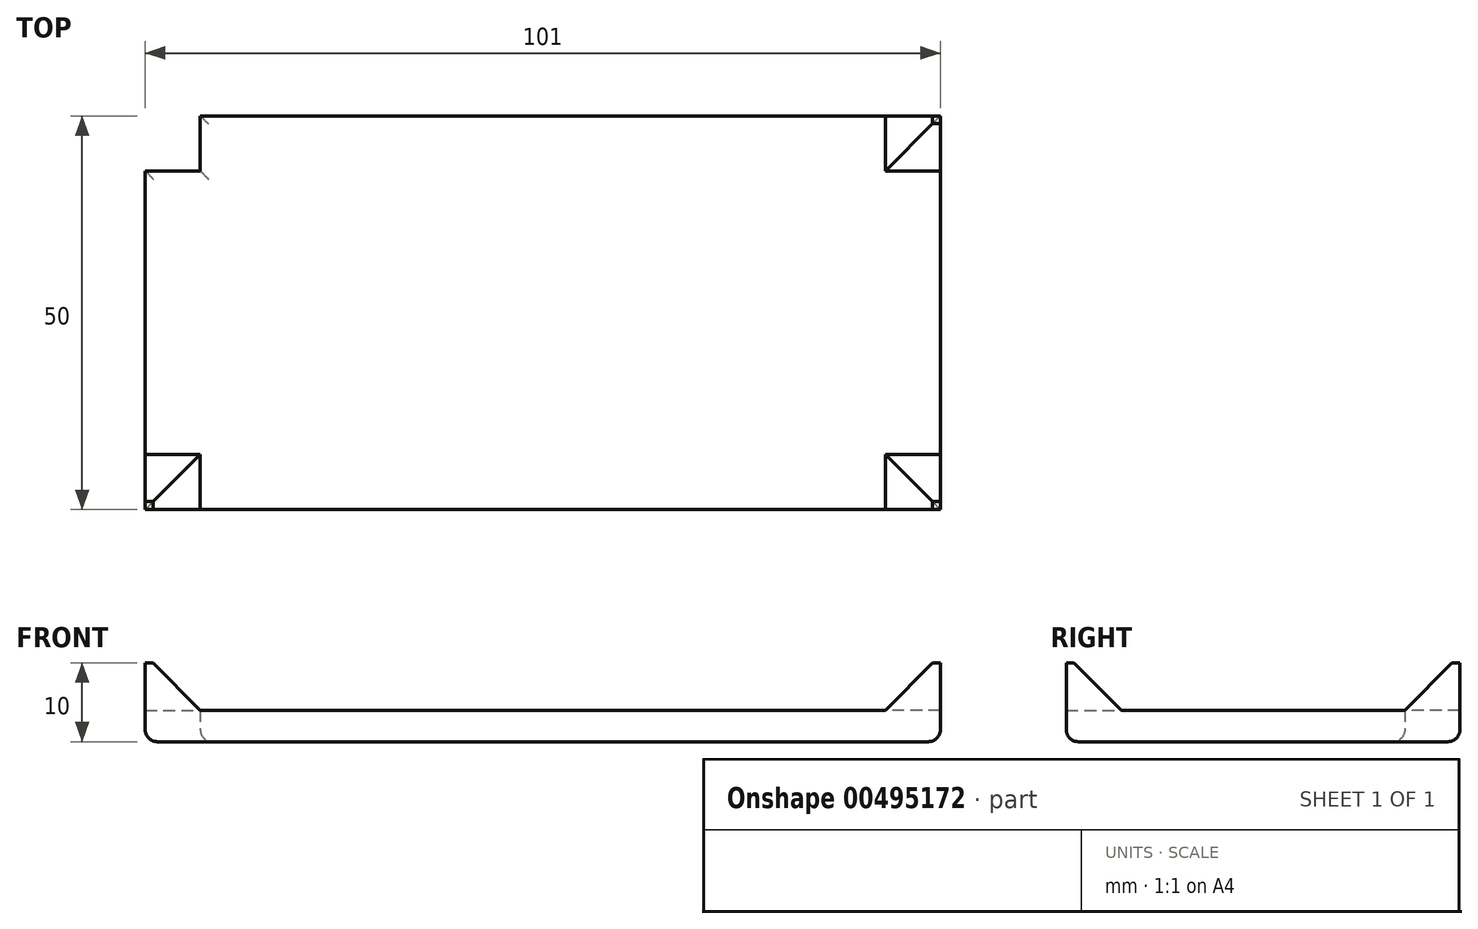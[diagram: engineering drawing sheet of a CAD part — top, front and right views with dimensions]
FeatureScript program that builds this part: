
annotation { "Feature Type Name" : "Feature", "Feature Type Description" : "" }
export const myFeature = defineFeature(function(context is Context, id is Id, definition is map)
    precondition{}
    {
        {
            var Q0;
            Q0=qCreatedBy(makeId("Top.planeOp"),FACE);
            var sketch = newSketch(context, id + "F0", { "sketchPlane" : qUnion([Q0])});
            skLineSegment(sketch, "E0.bottom", {"start": v(-50.5, 25) * mm, "end": v(50.5, 25) * mm});
            skLineSegment(sketch, "E0.top", {"start": v(-50.5, -25) * mm, "end": v(50.5, -25) * mm});
            skLineSegment(sketch, "E0.left", {"start": v(-50.5, 25) * mm, "end": v(-50.5, -25) * mm});
            skLineSegment(sketch, "E0.right", {"start": v(50.5, 25) * mm, "end": v(50.5, -25) * mm});
            skPoint(sketch, "E0.middle", {"position": v(0, 0) * mm});
            skLineSegment(sketch, "E1.bottom", {"start": v(-50.5, 25) * mm, "end": v(-43.5, 25) * mm});
            skLineSegment(sketch, "E1.top", {"start": v(-50.5, 18) * mm, "end": v(-43.5, 18) * mm});
            skLineSegment(sketch, "E1.left", {"start": v(-50.5, 25) * mm, "end": v(-50.5, 18) * mm});
            skLineSegment(sketch, "E1.right", {"start": v(-43.5, 25) * mm, "end": v(-43.5, 18) * mm});
            skLineSegment(sketch, "E2", {"start": v(-50.5, 18) * mm, "end": v(-50.5, 25) * mm, "construction": true});
            skLineSegment(sketch, "E3", {"start": v(-43.5, 25) * mm, "end": v(-50.5, 25) * mm, "construction": true});
            skLineSegment(sketch, "E4.MirrorCS", {"start": v(-50.5, -18) * mm, "end": v(-43.5, -18) * mm});
            skLineSegment(sketch, "E5.MirrorCS", {"start": v(-43.5, -25) * mm, "end": v(-43.5, -18) * mm});
            skLineSegment(sketch, "E6.MirrorCS", {"start": v(50.5, 18) * mm, "end": v(43.5, 18) * mm});
            skLineSegment(sketch, "E7.MirrorCS", {"start": v(43.5, 25) * mm, "end": v(43.5, 18) * mm});
            skLineSegment(sketch, "E8.MirrorCS", {"start": v(50.5, -18) * mm, "end": v(43.5, -18) * mm});
            skLineSegment(sketch, "E9.MirrorCS", {"start": v(43.5, -25) * mm, "end": v(43.5, -18) * mm});
            skSolve(sketch);
        }
        {
            var Q0;
            {var subQ3=sQuery(id+"F0.wireOp",EDGE,"E1.top");Q0=makeQuery(id+"F0.imprint","IMPRINT",FACE,{"disambiguationData":[TD([[makeQuery(id+"F0.imprint","IMPRINT",EDGE,{"derivedFrom":subQ3}),-1.0]])]});}
            extrude(context, id + "F1", {"entities" : qUnion([Q0]), "depth" : 4 * mm});
        }
        {
            var Q0;
            Q0=makeQuery(id+"F0.imprint","IMPRINT",FACE,{"disambiguationData":[TD([[makeQuery(id+"F0.imprint","IMPRINT",EDGE,{"derivedFrom":sQuery(id+"F0.wireOp",EDGE,"E1.bottom")}),-1.0]])]});
            var Q1;
            {var subQ4=sQuery(id+"F0.wireOp",EDGE,"E4.MirrorCS");Q1=makeQuery(id+"F0.imprint","IMPRINT",FACE,{"disambiguationData":[TD([[makeQuery(id+"F0.imprint","IMPRINT",EDGE,{"derivedFrom":subQ4}),-1.0]])]});}
            var Q2;
            {var subQ4=sQuery(id+"F0.wireOp",EDGE,"E6.MirrorCS");Q2=makeQuery(id+"F0.imprint","IMPRINT",FACE,{"disambiguationData":[TD([[makeQuery(id+"F0.imprint","IMPRINT",EDGE,{"derivedFrom":subQ4}),-1.0]])]});}
            var Q3;
            {var subQ4=sQuery(id+"F0.wireOp",EDGE,"E8.MirrorCS");Q3=makeQuery(id+"F0.imprint","IMPRINT",FACE,{"disambiguationData":[TD([[makeQuery(id+"F0.imprint","IMPRINT",EDGE,{"derivedFrom":subQ4}),1.0]])]});}
            extrude(context, id + "F2", {"entities" : qUnion([Q0, Q1, Q2, Q3]), "operationType" : NewBodyOperationType.ADD, "depth" : 10 * mm});
        }
        {
            var Q0;
            Q0=makeQuery(id+"F2.opExtrude","SWEPT_EDGE",EDGE,{"disambiguationData":[OSD([sQuery(id+"F0.wireOp",EDGE,"E1.top"),sQuery(id+"F0.wireOp",EDGE,"E1.right")])]});
            var Q1;
            Q1=makeQuery(id+"F2.opExtrude","CAP_EDGE",EDGE,{"disambiguationData":[OSD([sQuery(id+"F0.wireOp",EDGE,"E1.top")])],"isStart":false});
            var Q2;
            Q2=makeQuery(id+"F2.opExtrude","CAP_EDGE",EDGE,{"disambiguationData":[OSD([sQuery(id+"F0.wireOp",EDGE,"E1.right")])],"isStart":false});
            var Q3;
            Q3=makeQuery(id+"F2.opExtrude","CAP_EDGE",EDGE,{"disambiguationData":[OSD([sQuery(id+"F0.wireOp",EDGE,"E7.MirrorCS")])],"isStart":false});
            var Q4;
            Q4=makeQuery(id+"F2.opExtrude","CAP_EDGE",EDGE,{"disambiguationData":[OSD([sQuery(id+"F0.wireOp",EDGE,"E6.MirrorCS")])],"isStart":false});
            var Q5;
            Q5=makeQuery(id+"F2.opExtrude","CAP_EDGE",EDGE,{"disambiguationData":[OSD([sQuery(id+"F0.wireOp",EDGE,"E8.MirrorCS")])],"isStart":false});
            var Q6;
            Q6=makeQuery(id+"F2.opExtrude","CAP_EDGE",EDGE,{"disambiguationData":[OSD([sQuery(id+"F0.wireOp",EDGE,"E9.MirrorCS")])],"isStart":false});
            var Q7;
            Q7=makeQuery(id+"F2.opExtrude","CAP_EDGE",EDGE,{"disambiguationData":[OSD([sQuery(id+"F0.wireOp",EDGE,"E5.MirrorCS")])],"isStart":false});
            var Q8;
            Q8=makeQuery(id+"F2.opExtrude","CAP_EDGE",EDGE,{"disambiguationData":[OSD([sQuery(id+"F0.wireOp",EDGE,"E4.MirrorCS")])],"isStart":false});
            chamfer(context, id + "F3", {"entities" : qUnion([Q0, Q1, Q2, Q3, Q4, Q5, Q6, Q7, Q8]), "width" : 6 * mm, "tangentPropagation" : true});
        }
        {
            var Q0;
            {var subQ0=sQuery(id+"F0.wireOp",EDGE,"E1.right");var subQ1=sQuery(id+"F0.wireOp",EDGE,"E1.top");var subQ2=sQuery(id+"F0.wireOp",EDGE,"E9.MirrorCS");var subQ3=sQuery(id+"F0.wireOp",EDGE,"E8.MirrorCS");var subQ4=sQuery(id+"F0.wireOp",EDGE,"E0.right");var subQ5=sQuery(id+"F0.wireOp",EDGE,"E0.top");var subQ6=sQuery(id+"F0.wireOp",EDGE,"E5.MirrorCS");var subQ7=sQuery(id+"F0.wireOp",EDGE,"E4.MirrorCS");var subQ8=sQuery(id+"F0.wireOp",EDGE,"E0.left");var subQ9=sQuery(id+"F0.wireOp",EDGE,"E7.MirrorCS");var subQ10=sQuery(id+"F0.wireOp",EDGE,"E6.MirrorCS");var subQ11=sQuery(id+"F0.wireOp",EDGE,"E0.bottom");Q0=makeQuery(id+"F2.boolean.opBoolean","MERGE",FACE,{"derivedFrom":[makeQuery(id+"F1.opExtrude","CAP_FACE",FACE,{"disambiguationData":[OSD([subQ11,subQ5,subQ8,subQ4,subQ1,subQ0,subQ7,subQ6,subQ10,subQ9,subQ3,subQ2])],"isStart":true}),makeQuery(id+"F2.opExtrude","CAP_FACE",FACE,{"disambiguationData":[OSD([subQ11,subQ4,subQ10,subQ9])],"isStart":true}),makeQuery(id+"F2.opExtrude","CAP_FACE",FACE,{"disambiguationData":[OSD([subQ5,subQ8,subQ7,subQ6])],"isStart":true}),makeQuery(id+"F2.opExtrude","CAP_FACE",FACE,{"disambiguationData":[OSD([subQ5,subQ4,subQ3,subQ2])],"isStart":true}),makeQuery(id+"F2.opExtrude","CAP_FACE",FACE,{"disambiguationData":[OSD([sQuery(id+"F0.wireOp",EDGE,"E1.bottom"),subQ1,sQuery(id+"F0.wireOp",EDGE,"E1.left"),subQ0])],"isStart":true})]});}
            fillet(context, id + "F4", {"entities" : qUnion([Q0]), "radius" : 1.5 * mm, "tangentPropagation" : true, "allowEdgeOverflow" : false});
        }
    });
